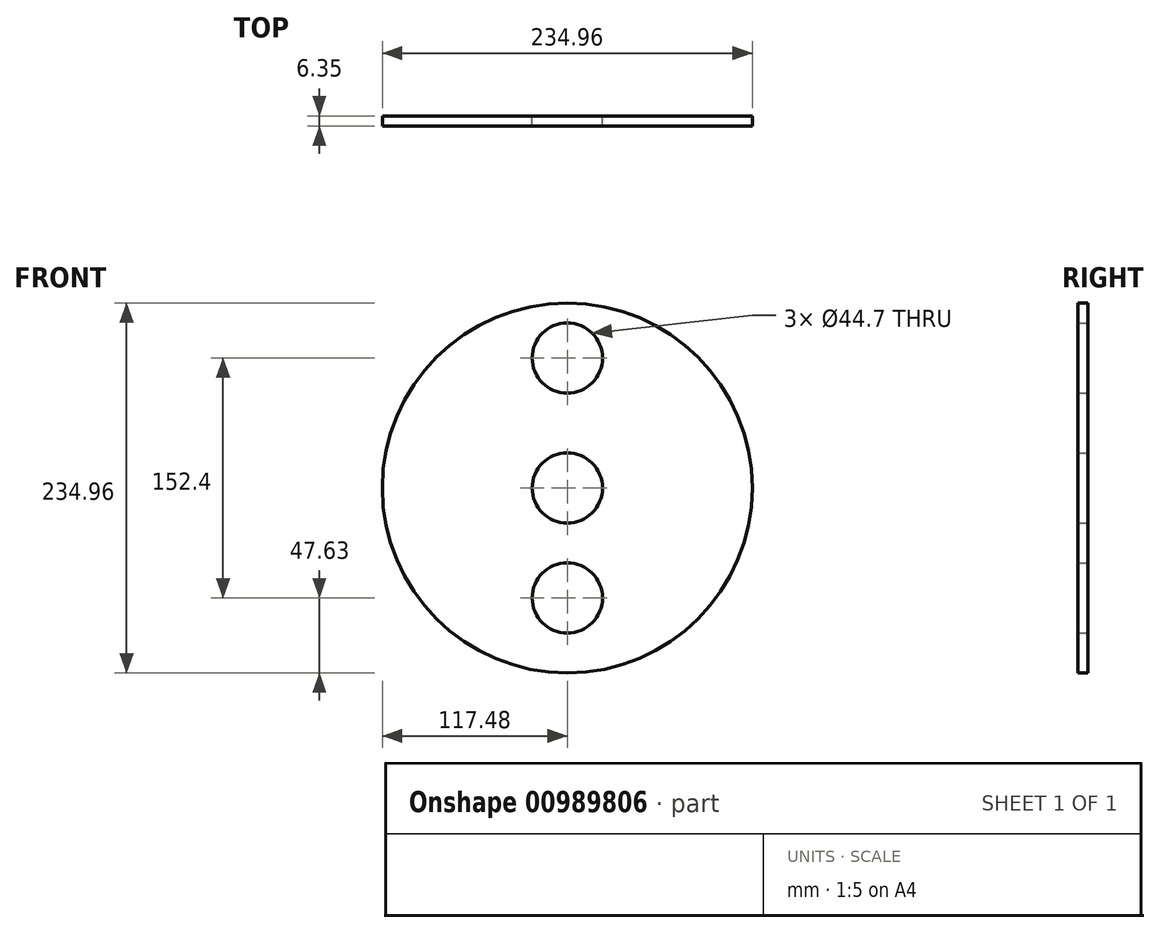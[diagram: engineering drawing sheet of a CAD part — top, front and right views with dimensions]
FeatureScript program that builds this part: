
annotation { "Feature Type Name" : "Feature", "Feature Type Description" : "" }
export const myFeature = defineFeature(function(context is Context, id is Id, definition is map)
    precondition{}
    {
        {
            var Q0;
            Q0=qCreatedBy(makeId("Front.planeOp"),FACE);
            var sketch = newSketch(context, id + "F0", { "sketchPlane" : qUnion([Q0])});
            skCircle(sketch, "E0", {"center": v(0, 0) * mm, "radius": 117.48 * mm});
            skSolve(sketch);
        }
        {
            var Q0;
            Q0=makeQuery(id+"F0.imprint","IMPRINT",FACE,{"disambiguationData":[TD([[makeQuery(id+"F0.imprint","IMPRINT",EDGE,{"derivedFrom":sQuery(id+"F0.wireOp",EDGE,"E0")}),1.0]])]});
            extrude(context, id + "F1", {"entities" : qUnion([Q0]), "depth" : 6.35 * mm, "offsetDistance" : 25.4 * mm});
        }
        {
            var Q0;
            Q0=qCreatedBy(makeId("Front.planeOp"),FACE);
            var sketch = newSketch(context, id + "F2", { "sketchPlane" : qUnion([Q0])});
            skCircle(sketch, "E1", {"center": v(0, 0) * mm, "radius": 117.48 * mm});
            skCircle(sketch, "E2", {"center": v(0, 0) * mm, "radius": 22.35 * mm});
            skCircle(sketch, "E3", {"center": v(0, 82.55) * mm, "radius": 22.35 * mm});
            skCircle(sketch, "E4.0.1.0", {"center": v(0, -69.85) * mm, "radius": 22.35 * mm});
            skLineSegment(sketch, "E4.direction1", {"start": v(0, 82.55) * mm, "end": v(19.46, 82.55) * mm, "construction": true});
            skLineSegment(sketch, "E4.direction2", {"start": v(0, 82.55) * mm, "end": v(0, -69.85) * mm, "construction": true});
            skSolve(sketch);
        }
        {
            var Q0;
            Q0=makeQuery(id+"F2.imprint","IMPRINT",FACE,{"disambiguationData":[TD([[makeQuery(id+"F2.imprint","IMPRINT",EDGE,{"derivedFrom":sQuery(id+"F2.wireOp",EDGE,"E1")}),1.0]])]});
            extrude(context, id + "F3", {"entities" : qUnion([Q0]), "depth" : 6.35 * mm, "offsetDistance" : 25.4 * mm});
        }
    });
